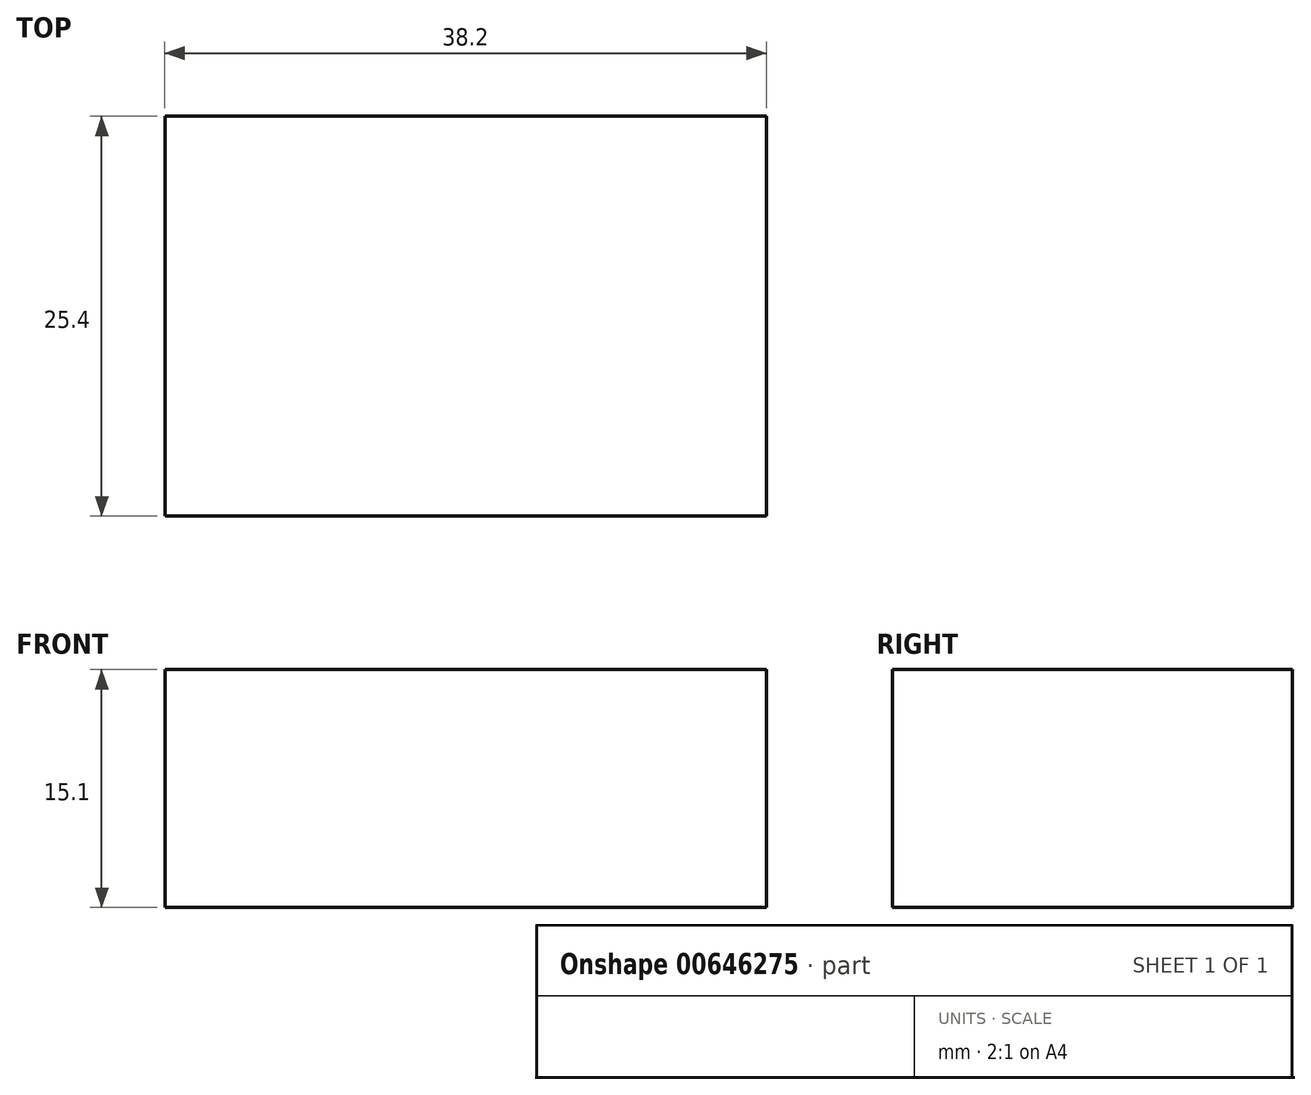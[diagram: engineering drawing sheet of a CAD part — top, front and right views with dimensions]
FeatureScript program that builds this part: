
annotation { "Feature Type Name" : "Feature", "Feature Type Description" : "" }
export const myFeature = defineFeature(function(context is Context, id is Id, definition is map)
    precondition{}
    {
        {
            var Q0;
            Q0=qCreatedBy(makeId("Front.planeOp"),FACE);
            var sketch = newSketch(context, id + "F0", { "sketchPlane" : qUnion([Q0])});
            skLineSegment(sketch, "E0.bottom", {"start": v(-16.87, 7.95) * mm, "end": v(21.33, 7.95) * mm});
            skLineSegment(sketch, "E0.top", {"start": v(-16.87, -7.15) * mm, "end": v(21.33, -7.15) * mm});
            skLineSegment(sketch, "E0.left", {"start": v(-16.87, 7.95) * mm, "end": v(-16.87, -7.15) * mm});
            skLineSegment(sketch, "E0.right", {"start": v(21.33, 7.95) * mm, "end": v(21.33, -7.15) * mm});
            skSolve(sketch);
        }
        {
            var Q0;
            Q0=makeQuery(id+"F0.imprint","IMPRINT",FACE,{"disambiguationData":[TD([[makeQuery(id+"F0.imprint","IMPRINT",EDGE,{"derivedFrom":sQuery(id+"F0.wireOp",EDGE,"E0.bottom")}),-1.0]])]});
            extrude(context, id + "F1", {"entities" : qUnion([Q0]), "depth" : 25.4 * mm, "offsetDistance" : 25.4 * mm});
        }
    });
